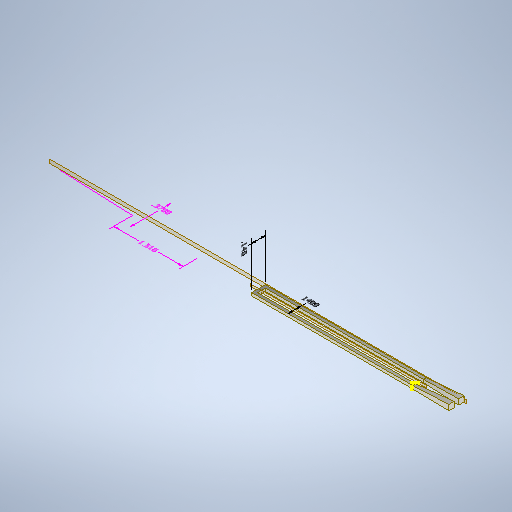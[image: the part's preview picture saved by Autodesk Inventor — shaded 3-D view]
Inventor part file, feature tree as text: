
AUTODESK INVENTOR PART (.ipt)
format: ipt  version: 2025.2 (Build 292293000, 293)  size: 307,712 bytes
history: native  units: in
note: dims shown in document units (in); Inventor stores cm internally (conversion verified against a paired STEP export)
features: other x6, plane x4, sketch x4, sweep x1, loft x1, mirror x1, projected_geometry x1
ambient origin geometry x8: Origin, YZ Plane, XZ Plane, XY Plane, X Axis, Y Axis, Z Axis, Center Point
bodies: Solid1 (feature_tree)
feature tree (18):
  other  "Annotations"
  sweep  "Sweep1"
  plane  "Work Plane1"
  plane  "Work Plane2"
  plane  "Work Plane4"
  sketch  "Sketch15"  dims[d86=-0.1175in]
  sketch  "Sketch16"  dims[d89=0.1in d90=0.0in d91=0.0in d92=0.0in d98=0.03in d99=0.03in d100=0.055in d102=0.055in d104=0.0in d109=0.0in d110=90.0deg d111=0.0in d112=90.0deg d116=-0.07in d113=0.0in d114=0.3937in d115=0.14in d117=0.086in d118=0.3123in d119=0.14in d42=0.2341in d43=0.169in d44=0.37in d48=0.2141in d49=0.2512in d50=1.51in]
  loft  "Loft3"
  plane  "Work Plane5"
  mirror  "Mirror3"
  sketch  "Sketch1"  dims[d6=0.0in d7=0.0in d11=0.375in d19=-0.25in]
  sketch  "Sketch2"  dims[d69=1.625in d70=1.625in]
  projected_geometry  "Projected Loop1"
  other  "Edges4"
  other  "Linear Dimension 1"
  other  "Linear Dimension 3"
  other  "Linear Dimension 4"
  other  "Linear Dimension 5"
